# Revit family: Building-IEC309Connections-GEWISS-COMBIBLOC_BOARD_1SOCKET
name_source: partatom
category: Apparecchi elettrici
units: mm (PartAtom-declared; Revit-internal decimal feet)

## family parameters
Condiviso = No
Host = Superficie
Mantenere orientamento annotazione = Sì
Punto di calcolo locali = Sì
Quota connettore circolare = Usa diametro
Taglio con vuoti quando caricato = No
Tipo di parte = Normale

## types (1)
- GW66491 - BOARD IP55 EMPTY VERT. COMBIBLOC 1 SOCK
    Accessories supplied = 70 °C
    Accordance with Standards = EN 62208
    Catalogue = BUILDING
    Colour = Grey RAL 7035
    Descrizione = BOARD IP55 EMPTY VERT. COMBIBLOC 1 SOCK
    Dispersible power (W) = 10
    Electrocod = 0321
    For socket-outlets = Compact
    Glow Wire Test = 650°C
    Glow wire test: = Empty
    IDF = c5e44f26-db2e-429e-81e4-909959e80605
    IDT = 7256ea7ecdc24b538c455d8827a18355
    IP degree = IP55
    Installation type = Surface-mounting
    Insulation class = II
    Modello = GW66491
    No. IB socket-outlets houseable = 1 COMBIBLOC 16/32A
    No. of blank lids supplied = None
    No. of modules EN 50022 = 4
    Operating temperature: = -25 +40 °C
    Produttore = GEWISS S.p.A.
    Prospetto di default = 1219 mm
    SEO = Board
    STRUTTURA = RAL - 7035
    STRUTTURA ALTA = Poche
    Shock resistance = IK08
    Spostamento_S = 1420 mm  [stored 4.65879 ft]
    Technical sheet = https://www.gewiss.com
    Thermo-pressure with ball = 70
    URL = https://www.gewiss.com
    Version file RFA = 21.10
    Version type = Empty

note: source unit labels omitted for Thermo-pressure with ball — the stored unit's dimension contradicts the parameter name (converter mislabeling)

note: [stored X ft] marks values corroborated as IEEE doubles in the binary element streams (Revit-internal decimal feet)

## geometry (parser evidence)
native form markers: Sweep x2
no freeform markers — native parametric forms only
